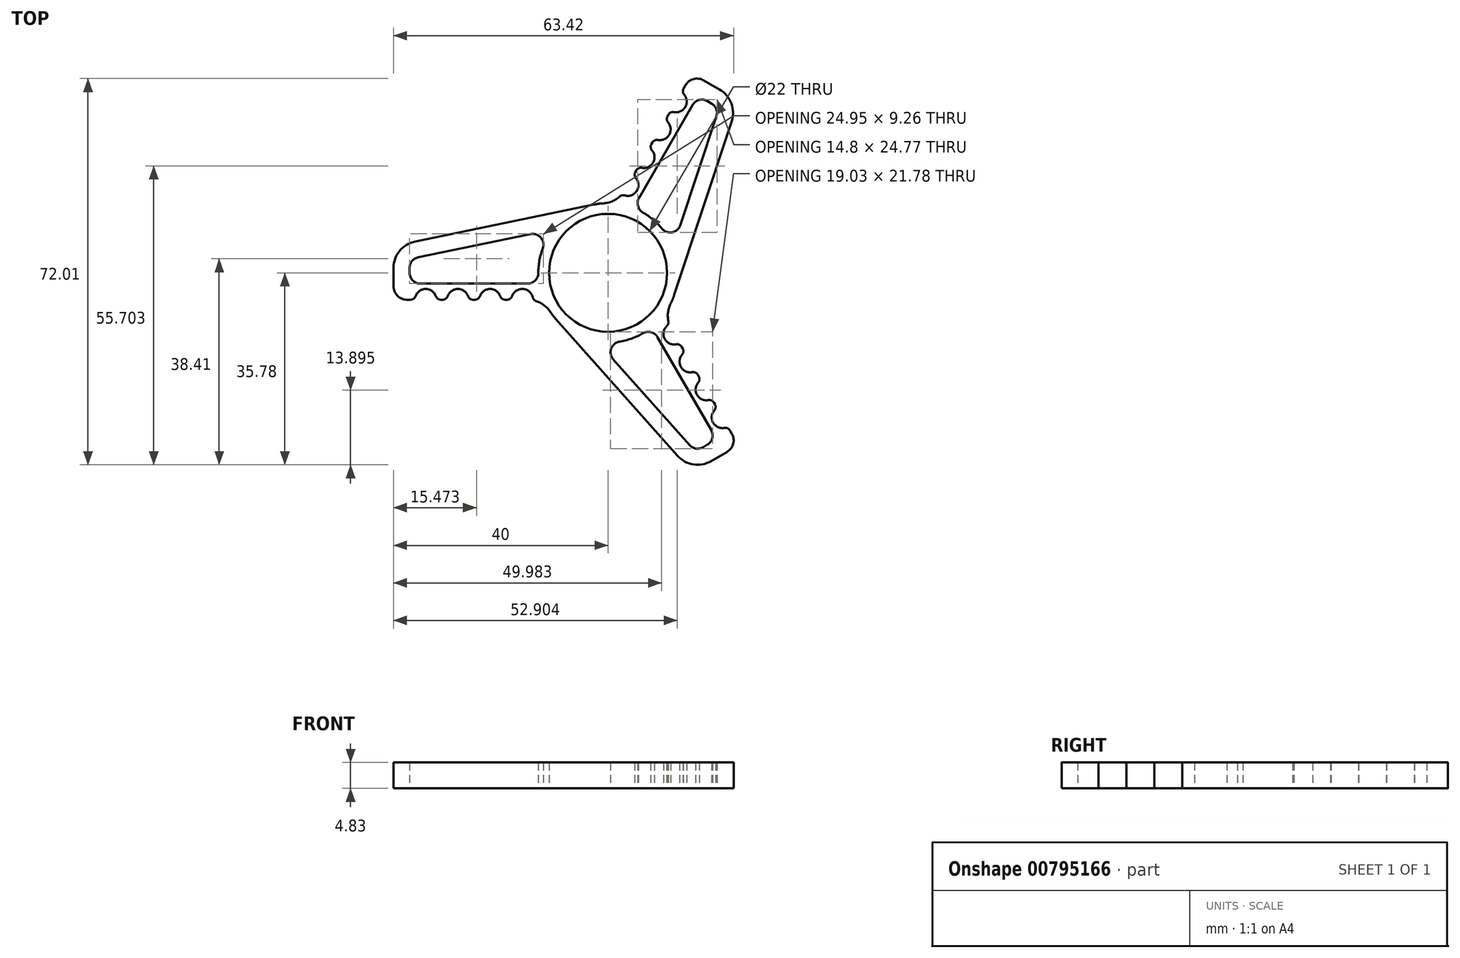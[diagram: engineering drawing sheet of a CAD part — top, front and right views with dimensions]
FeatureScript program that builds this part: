
annotation { "Feature Type Name" : "Feature", "Feature Type Description" : "" }
export const myFeature = defineFeature(function(context is Context, id is Id, definition is map)
    precondition{}
    {
        {
            var Q0;
            Q0=qCreatedBy(makeId("Top.planeOp"),FACE);
            var sketch = newSketch(context, id + "F0", { "sketchPlane" : qUnion([Q0])});
            skCircle(sketch, "E0", {"center": v(0, 0) * mm, "radius": 11 * mm});
            skArc(sketch, "E1", {"start": v(-12.17, 4.56) * mm, "mid": v(-12.8, 2.32) * mm, "end": v(-13, 0) * mm});
            skLineSegment(sketch, "E2", {"start": v(-40, 0.93) * mm, "end": v(-40, -2.5) * mm});
            skLineSegment(sketch, "E3", {"start": v(-36.01, 5.82) * mm, "end": v(-2.63, 12.73) * mm});
            skLineSegment(sketch, "E4", {"start": v(-37.5, -5) * mm, "end": v(-36.83, -5) * mm});
            skPoint(sketch, "E5.visualSharp", {"position": v(-40, 5) * mm});
            skArc(sketch, "E5.filletArc", {"start": v(-36.01, 5.82) * mm, "mid": v(-38.88, 4.09) * mm, "end": v(-40, 0.93) * mm});
            skPoint(sketch, "E6.visualSharp", {"position": v(-40, -5) * mm});
            skArc(sketch, "E6.filletArc", {"start": v(-40, -2.5) * mm, "mid": v(-39.27, -4.27) * mm, "end": v(-37.5, -5) * mm});
            skPoint(sketch, "E7.visualSharp", {"position": v(-12, -5) * mm});
            skArc(sketch, "E7.filletArc", {"start": v(-10.8, -7.22) * mm, "mid": v(-11.94, -6.02) * mm, "end": v(-13.4, -5.25) * mm});
            skArc(sketch, "E8", {"start": v(-32.11, -4.33) * mm, "mid": v(-34, -3) * mm, "end": v(-35.89, -4.33) * mm});
            skArc(sketch, "E9.1.0.0", {"start": v(-26.11, -4.33) * mm, "mid": v(-28, -3) * mm, "end": v(-29.89, -4.33) * mm});
            skArc(sketch, "E9.2.0.0", {"start": v(-20.11, -4.33) * mm, "mid": v(-22, -3) * mm, "end": v(-23.89, -4.33) * mm});
            skArc(sketch, "E9.3.0.0", {"start": v(-14.05, -4.54) * mm, "mid": v(-15.9, -3) * mm, "end": v(-17.89, -4.33) * mm});
            skLineSegment(sketch, "E10.3", {"start": v(-35.4, 2.89) * mm, "end": v(-14.45, 7.22) * mm});
            skLineSegment(sketch, "E10.4", {"start": v(-35, -2) * mm, "end": v(-15, -2) * mm});
            skLineSegment(sketch, "E10.5", {"start": v(-37, 0.93) * mm, "end": v(-37, 0) * mm});
            skArc(sketch, "E11.trimOffspring", {"start": v(-10.8, -7.22) * mm, "mid": v(-10.28, -7.95) * mm, "end": v(-9.7, -8.65) * mm});
            skPoint(sketch, "E12.visualSharp", {"position": v(-37, 2.56) * mm});
            skArc(sketch, "E12.filletArc", {"start": v(-35.4, 2.89) * mm, "mid": v(-36.55, 2.2) * mm, "end": v(-37, 0.93) * mm});
            skPoint(sketch, "E13.visualSharp", {"position": v(-37, -2) * mm});
            skArc(sketch, "E13.filletArc", {"start": v(-37, 0) * mm, "mid": v(-36.41, -1.41) * mm, "end": v(-35, -2) * mm});
            skArc(sketch, "E14.filletArc", {"start": v(-15, -2) * mm, "mid": v(-13.59, -1.41) * mm, "end": v(-13, 0) * mm});
            skPoint(sketch, "E15.visualSharp", {"position": v(-10.16, 8.1) * mm});
            skArc(sketch, "E15.filletArc", {"start": v(-12.17, 4.56) * mm, "mid": v(-12.53, 6.56) * mm, "end": v(-14.45, 7.22) * mm});
            skLineSegment(sketch, "E16.trimOffspring", {"start": v(-25.17, -5) * mm, "end": v(-24.83, -5) * mm});
            skLineSegment(sketch, "E17.trimOffspring", {"start": v(-19.17, -5) * mm, "end": v(-18.83, -5) * mm});
            skPoint(sketch, "E18.visualSharp", {"position": v(-36, -5) * mm});
            skArc(sketch, "E18.filletArc", {"start": v(-36.83, -5) * mm, "mid": v(-36.25, -4.82) * mm, "end": v(-35.89, -4.33) * mm});
            skPoint(sketch, "E19.visualSharp", {"position": v(-32, -5) * mm});
            skArc(sketch, "E19.filletArc", {"start": v(-32.11, -4.33) * mm, "mid": v(-31.75, -4.82) * mm, "end": v(-31.17, -5) * mm});
            skPoint(sketch, "E20.visualSharp", {"position": v(-30, -5) * mm});
            skArc(sketch, "E20.filletArc", {"start": v(-30.83, -5) * mm, "mid": v(-30.25, -4.82) * mm, "end": v(-29.89, -4.33) * mm});
            skPoint(sketch, "E21.visualSharp", {"position": v(-26, -5) * mm});
            skArc(sketch, "E21.filletArc", {"start": v(-26.11, -4.33) * mm, "mid": v(-25.75, -4.82) * mm, "end": v(-25.17, -5) * mm});
            skPoint(sketch, "E22.visualSharp", {"position": v(-24, -5) * mm});
            skArc(sketch, "E22.filletArc", {"start": v(-24.83, -5) * mm, "mid": v(-24.25, -4.82) * mm, "end": v(-23.89, -4.33) * mm});
            skPoint(sketch, "E23.visualSharp", {"position": v(-20, -5) * mm});
            skArc(sketch, "E23.filletArc", {"start": v(-20.11, -4.33) * mm, "mid": v(-19.75, -4.82) * mm, "end": v(-19.17, -5) * mm});
            skPoint(sketch, "E24.visualSharp", {"position": v(-18, -5) * mm});
            skArc(sketch, "E24.filletArc", {"start": v(-18.83, -5) * mm, "mid": v(-18.25, -4.82) * mm, "end": v(-17.89, -4.33) * mm});
            skPoint(sketch, "E25.visualSharp", {"position": v(-14, -5.1) * mm});
            skArc(sketch, "E25.filletArc", {"start": v(-14.05, -4.54) * mm, "mid": v(-13.82, -4.98) * mm, "end": v(-13.4, -5.25) * mm});
            skLineSegment(sketch, "E26", {"start": v(-31.17, -5) * mm, "end": v(-30.83, -5) * mm});
            skArc(sketch, "E27.trimOffspring", {"start": v(11.66, -5.75) * mm, "mid": v(12.03, -4.93) * mm, "end": v(12.34, -4.08) * mm});
            skArc(sketch, "E28.1.0", {"start": v(9.23, -12) * mm, "mid": v(8.02, -11.06) * mm, "end": v(6.5, -11.26) * mm});
            skArc(sketch, "E28.1.1", {"start": v(2.14, -12.82) * mm, "mid": v(0.58, -14.13) * mm, "end": v(0.97, -16.13) * mm});
            skPoint(sketch, "E28.1.2", {"position": v(16.33, -18.28) * mm});
            skPoint(sketch, "E28.1.3", {"position": v(10.33, -7.9) * mm});
            skPoint(sketch, "E28.1.4", {"position": v(20.33, -25.21) * mm});
            skPoint(sketch, "E28.1.5", {"position": v(20.23, -31.04) * mm});
            skPoint(sketch, "E28.1.6", {"position": v(16.29, -33.32) * mm});
            skPoint(sketch, "E28.1.7", {"position": v(13.33, -13.09) * mm});
            skPoint(sketch, "E28.1.8", {"position": v(14.33, -14.82) * mm});
            skPoint(sketch, "E28.1.9", {"position": v(19.33, -23.48) * mm});
            skLineSegment(sketch, "E28.1.10", {"start": v(19.23, -29.31) * mm, "end": v(9.23, -12) * mm});
            skArc(sketch, "E28.1.11", {"start": v(2.14, -12.82) * mm, "mid": v(4.39, -12.24) * mm, "end": v(6.5, -11.26) * mm});
            skLineSegment(sketch, "E28.1.12", {"start": v(19.2, -35.1) * mm, "end": v(22.17, -33.4) * mm});
            skLineSegment(sketch, "E28.1.13", {"start": v(12.96, -34.1) * mm, "end": v(-9.7, -8.65) * mm});
            skArc(sketch, "E28.1.14", {"start": v(12.96, -34.1) * mm, "mid": v(15.9, -35.71) * mm, "end": v(19.2, -35.1) * mm});
            skPoint(sketch, "E28.1.15", {"position": v(15.67, -37.14) * mm});
            skArc(sketch, "E28.1.16", {"start": v(19.8, -25.65) * mm, "mid": v(19.6, -27.94) * mm, "end": v(21.7, -28.91) * mm});
            skArc(sketch, "E28.1.17", {"start": v(16.8, -20.45) * mm, "mid": v(16.6, -22.75) * mm, "end": v(18.7, -23.72) * mm});
            skArc(sketch, "E28.1.18", {"start": v(13.8, -15.25) * mm, "mid": v(13.6, -17.55) * mm, "end": v(15.7, -18.52) * mm});
            skArc(sketch, "E28.1.19", {"start": v(10.96, -9.9) * mm, "mid": v(10.55, -12.26) * mm, "end": v(12.7, -13.32) * mm});
            skLineSegment(sketch, "E28.1.20", {"start": v(15.2, -32.1) * mm, "end": v(0.97, -16.13) * mm});
            skPoint(sketch, "E28.1.21", {"position": v(11.41, -9.58) * mm});
            skPoint(sketch, "E28.1.22", {"position": v(-1.94, -12.85) * mm});
            skPoint(sketch, "E28.1.23", {"position": v(17.33, -20.02) * mm});
            skPoint(sketch, "E28.1.24", {"position": v(24.33, -32.14) * mm});
            skPoint(sketch, "E28.1.26", {"position": v(22.33, -28.68) * mm});
            skArc(sketch, "E28.1.27", {"start": v(22.17, -33.4) * mm, "mid": v(23.33, -31.87) * mm, "end": v(23.08, -29.98) * mm});
            skArc(sketch, "E28.1.28", {"start": v(11.66, -5.75) * mm, "mid": v(11.18, -7.33) * mm, "end": v(11.25, -8.97) * mm});
            skArc(sketch, "E28.1.29", {"start": v(15.2, -32.1) * mm, "mid": v(16.38, -32.75) * mm, "end": v(17.7, -32.5) * mm});
            skArc(sketch, "E28.1.30", {"start": v(18.5, -32.04) * mm, "mid": v(19.43, -30.83) * mm, "end": v(19.23, -29.31) * mm});
            skArc(sketch, "E28.1.31", {"start": v(16.8, -20.45) * mm, "mid": v(17.05, -19.9) * mm, "end": v(16.92, -19.3) * mm});
            skArc(sketch, "E28.1.32", {"start": v(13.74, -13.8) * mm, "mid": v(13.3, -13.4) * mm, "end": v(12.7, -13.32) * mm});
            skArc(sketch, "E28.1.33", {"start": v(22.74, -29.4) * mm, "mid": v(22.3, -28.99) * mm, "end": v(21.7, -28.91) * mm});
            skArc(sketch, "E28.1.34", {"start": v(16.74, -19) * mm, "mid": v(16.3, -18.6) * mm, "end": v(15.7, -18.52) * mm});
            skArc(sketch, "E28.1.35", {"start": v(13.8, -15.25) * mm, "mid": v(14.05, -14.7) * mm, "end": v(13.92, -14.1) * mm});
            skLineSegment(sketch, "E28.1.36", {"start": v(16.92, -19.3) * mm, "end": v(16.74, -19) * mm});
            skArc(sketch, "E28.1.37", {"start": v(10.96, -9.9) * mm, "mid": v(11.22, -9.48) * mm, "end": v(11.25, -8.97) * mm});
            skLineSegment(sketch, "E28.1.38", {"start": v(13.92, -14.1) * mm, "end": v(13.74, -13.8) * mm});
            skLineSegment(sketch, "E28.1.39", {"start": v(19.92, -24.5) * mm, "end": v(19.74, -24.2) * mm});
            skLineSegment(sketch, "E28.1.40", {"start": v(17.7, -32.5) * mm, "end": v(18.5, -32.04) * mm});
            skLineSegment(sketch, "E28.1.41", {"start": v(23.08, -29.98) * mm, "end": v(22.74, -29.4) * mm});
            skArc(sketch, "E28.1.42", {"start": v(19.8, -25.65) * mm, "mid": v(20.05, -25.09) * mm, "end": v(19.92, -24.5) * mm});
            skArc(sketch, "E28.1.43", {"start": v(19.74, -24.2) * mm, "mid": v(19.3, -23.8) * mm, "end": v(18.7, -23.72) * mm});
            skArc(sketch, "E28.2.0", {"start": v(5.77, 14) * mm, "mid": v(5.57, 12.47) * mm, "end": v(6.5, 11.26) * mm});
            skArc(sketch, "E28.2.1", {"start": v(10.04, 8.26) * mm, "mid": v(11.95, 7.57) * mm, "end": v(13.48, 8.9) * mm});
            skPoint(sketch, "E28.2.2", {"position": v(7.67, 23.28) * mm});
            skPoint(sketch, "E28.2.3", {"position": v(1.67, 12.9) * mm});
            skPoint(sketch, "E28.2.4", {"position": v(11.67, 30.21) * mm});
            skPoint(sketch, "E28.2.5", {"position": v(16.77, 33.04) * mm});
            skPoint(sketch, "E28.2.6", {"position": v(20.71, 30.76) * mm});
            skPoint(sketch, "E28.2.7", {"position": v(4.67, 18.09) * mm});
            skPoint(sketch, "E28.2.8", {"position": v(5.67, 19.82) * mm});
            skPoint(sketch, "E28.2.9", {"position": v(10.67, 28.48) * mm});
            skLineSegment(sketch, "E28.2.10", {"start": v(15.77, 31.31) * mm, "end": v(5.77, 14) * mm});
            skArc(sketch, "E28.2.11", {"start": v(10.04, 8.26) * mm, "mid": v(8.4, 9.92) * mm, "end": v(6.5, 11.26) * mm});
            skLineSegment(sketch, "E28.2.12", {"start": v(20.8, 34.18) * mm, "end": v(17.83, 35.9) * mm});
            skLineSegment(sketch, "E28.2.13", {"start": v(23.05, 28.28) * mm, "end": v(12.34, -4.08) * mm});
            skArc(sketch, "E28.2.14", {"start": v(23.05, 28.28) * mm, "mid": v(22.98, 31.63) * mm, "end": v(20.8, 34.18) * mm});
            skPoint(sketch, "E28.2.15", {"position": v(24.33, 32.14) * mm});
            skArc(sketch, "E28.2.16", {"start": v(12.3, 29.98) * mm, "mid": v(14.4, 30.94) * mm, "end": v(14.2, 33.24) * mm});
            skArc(sketch, "E28.2.17", {"start": v(9.3, 24.78) * mm, "mid": v(11.4, 25.75) * mm, "end": v(11.2, 28.05) * mm});
            skArc(sketch, "E28.2.18", {"start": v(6.3, 19.59) * mm, "mid": v(8.4, 20.55) * mm, "end": v(8.2, 22.85) * mm});
            skArc(sketch, "E28.2.19", {"start": v(3.1, 14.44) * mm, "mid": v(5.35, 15.27) * mm, "end": v(5.2, 17.66) * mm});
            skLineSegment(sketch, "E28.2.20", {"start": v(20.2, 29.22) * mm, "end": v(13.48, 8.9) * mm});
            skPoint(sketch, "E28.2.21", {"position": v(2.59, 14.67) * mm});
            skPoint(sketch, "E28.2.22", {"position": v(12.1, 4.74) * mm});
            skPoint(sketch, "E28.2.23", {"position": v(8.67, 25.02) * mm});
            skPoint(sketch, "E28.2.24", {"position": v(15.67, 37.14) * mm});
            skPoint(sketch, "E28.2.26", {"position": v(13.67, 33.68) * mm});
            skArc(sketch, "E28.2.27", {"start": v(17.83, 35.9) * mm, "mid": v(15.94, 36.14) * mm, "end": v(14.42, 34.98) * mm});
            skArc(sketch, "E28.2.28", {"start": v(-0.85, 12.97) * mm, "mid": v(0.75, 13.35) * mm, "end": v(2.15, 14.23) * mm});
            skArc(sketch, "E28.2.29", {"start": v(20.2, 29.22) * mm, "mid": v(20.17, 30.56) * mm, "end": v(19.3, 31.58) * mm});
            skArc(sketch, "E28.2.30", {"start": v(18.5, 32.04) * mm, "mid": v(16.98, 32.24) * mm, "end": v(15.77, 31.31) * mm});
            skArc(sketch, "E28.2.31", {"start": v(9.3, 24.78) * mm, "mid": v(8.7, 24.7) * mm, "end": v(8.26, 24.3) * mm});
            skArc(sketch, "E28.2.32", {"start": v(5.08, 18.8) * mm, "mid": v(4.95, 18.21) * mm, "end": v(5.2, 17.66) * mm});
            skArc(sketch, "E28.2.33", {"start": v(14.08, 34.4) * mm, "mid": v(13.95, 33.8) * mm, "end": v(14.2, 33.24) * mm});
            skArc(sketch, "E28.2.34", {"start": v(8.08, 24) * mm, "mid": v(7.95, 23.41) * mm, "end": v(8.2, 22.85) * mm});
            skArc(sketch, "E28.2.35", {"start": v(6.3, 19.59) * mm, "mid": v(5.7, 19.51) * mm, "end": v(5.26, 19.1) * mm});
            skLineSegment(sketch, "E28.2.36", {"start": v(8.26, 24.3) * mm, "end": v(8.08, 24) * mm});
            skArc(sketch, "E28.2.37", {"start": v(3.1, 14.44) * mm, "mid": v(2.6, 14.46) * mm, "end": v(2.15, 14.23) * mm});
            skLineSegment(sketch, "E28.2.38", {"start": v(5.26, 19.1) * mm, "end": v(5.08, 18.8) * mm});
            skLineSegment(sketch, "E28.2.39", {"start": v(11.26, 29.5) * mm, "end": v(11.08, 29.2) * mm});
            skLineSegment(sketch, "E28.2.40", {"start": v(19.3, 31.58) * mm, "end": v(18.5, 32.04) * mm});
            skLineSegment(sketch, "E28.2.41", {"start": v(14.42, 34.98) * mm, "end": v(14.08, 34.4) * mm});
            skArc(sketch, "E28.2.42", {"start": v(12.3, 29.98) * mm, "mid": v(11.7, 29.9) * mm, "end": v(11.26, 29.5) * mm});
            skArc(sketch, "E28.2.43", {"start": v(11.08, 29.2) * mm, "mid": v(10.95, 28.6) * mm, "end": v(11.2, 28.05) * mm});
            skArc(sketch, "E29.trimOffspring", {"start": v(-0.85, 12.97) * mm, "mid": v(-1.75, 12.88) * mm, "end": v(-2.63, 12.73) * mm});
            skArc(sketch, "E30.trimOffspring", {"start": v(2.14, -12.82) * mm, "mid": v(2.39, -12.78) * mm, "end": v(2.63, -12.73) * mm});
            skSolve(sketch);
        }
        {
            var Q0;
            Q0=makeQuery(id+"F0.imprint","IMPRINT",FACE,{"disambiguationData":[TD([[makeQuery(id+"F0.imprint","IMPRINT",EDGE,{"derivedFrom":sQuery(id+"F0.wireOp",EDGE,"E0")}),-1.0]])]});
            extrude(context, id + "F1", {"entities" : qUnion([Q0]), "depth" : 4.83 * mm, "offsetDistance" : 25 * mm});
        }
    });
